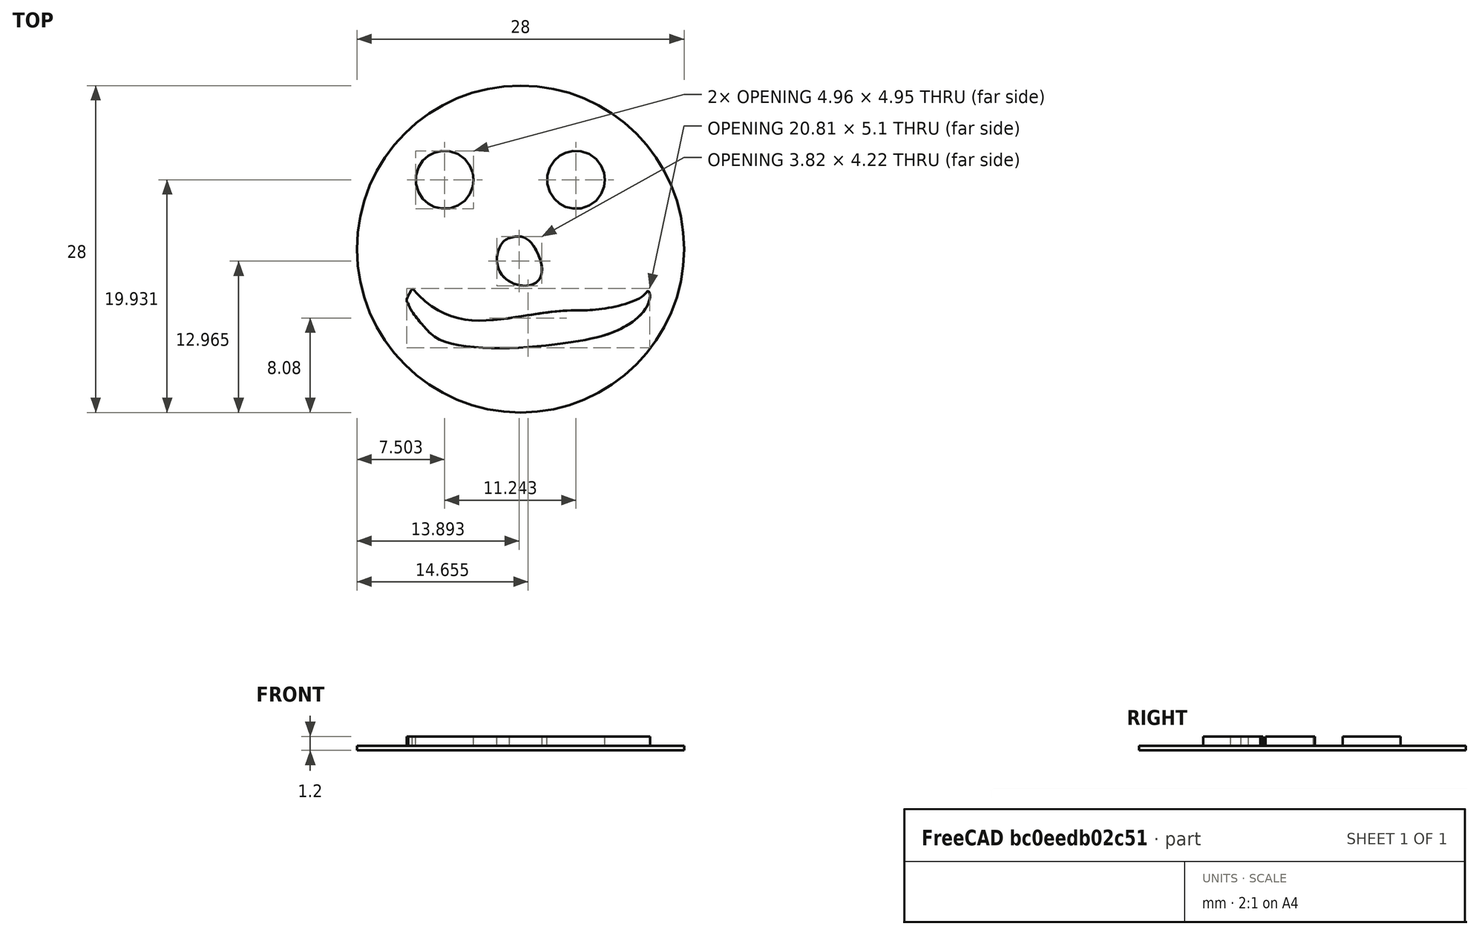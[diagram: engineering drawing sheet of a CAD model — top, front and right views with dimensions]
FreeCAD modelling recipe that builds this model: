
FCSTD DOCUMENT  (FreeCAD 0.18R14996 (Git))
Label: Medallion Face Test Rev B
License: All rights reserved
LicenseURL: http://en.wikipedia.org/wiki/All_rights_reserved
objects: Sketcher::SketchObject×2, PartDesign::Pad×2, Part::Part2DObjectPython×1, PartDesign::Body×1
note: 8 computed .brp shape members not serialized (recipe doc carries the construction recipe); baked Part::Feature solids carry a one-line shape summary decoded from their .brp

FEATURE [Sketcher::SketchObject] Sketch  label="Face Base Profile"
  MapMode = 5
  Support = -> [XY_Plane]
  sketch-geometry (1):
    g0: Circle CenterX=0 CenterY=0 CenterZ=0 NormalX=0 NormalY=0 NormalZ=1 AngleXU=0 Radius=14
  constraints (2):
    c: Coincident(g0,g-1)
    c: Radius(g0) = 14
FEATURE [PartDesign::Pad] Pad  label="Face Base"
  Length = 0.4
  Length2 = 100
  Profile = -> Sketch
  Type = 0
FEATURE [Sketcher::SketchObject] Sketch005
  Placement = pos=(-86.4048,117.218,0) rot=(0,0,1;0rad)
  sketch-geometry (11):
    g0: BSplineCurve PolesCount=7 KnotsCount=4 Degree=2 IsPeriodic=0
    g1: BSplineCurve PolesCount=4 KnotsCount=2 Degree=3 IsPeriodic=0
    g2: BSplineCurve PolesCount=4 KnotsCount=2 Degree=3 IsPeriodic=0
    g3: BSplineCurve PolesCount=4 KnotsCount=2 Degree=3 IsPeriodic=0
    g4: BSplineCurve PolesCount=7 KnotsCount=4 Degree=2 IsPeriodic=0
    g5: BSplineCurve PolesCount=4 KnotsCount=2 Degree=3 IsPeriodic=0
    g6: BSplineCurve PolesCount=4 KnotsCount=2 Degree=3 IsPeriodic=0
    g7: BSplineCurve PolesCount=4 KnotsCount=2 Degree=3 IsPeriodic=0
    g8: BSplineCurve PolesCount=4 KnotsCount=2 Degree=3 IsPeriodic=0
    g9: BSplineCurve PolesCount=4 KnotsCount=2 Degree=3 IsPeriodic=0
    g10: BSplineCurve PolesCount=4 KnotsCount=2 Degree=3 IsPeriodic=0
  constraints (9):
    c: Coincident(g1,g2)
    c: Coincident(g2,g3)
    c: Coincident(g3,g1)
    c: Coincident(g5,g6)
    c: Coincident(g6,g7)
    c: Coincident(g7,g8)
    c: Coincident(g8,g9)
    c: Coincident(g9,g10)
    c: Coincident(g10,g5)
FEATURE [Part::Part2DObjectPython] Clone2D  label="Sketch005 (2D)"  # Draft 2D object (typed FeaturePython)
  Fuse = false
  Objects = -> [Sketch005]
  Placement = pos=(-15.3624,20.0267,0) rot=(0,0,1;0rad)
  Scale = (0.18,0.18,0)
FEATURE [PartDesign::Pad] Pad001  label="Pattern Emboss"
  BaseFeature = -> Pad
  Length = 1.2
  Length2 = 100
  Profile = -> Clone2D
  Type = 0
FEATURE [PartDesign::Body] Body
  Group = -> [Sketch,Pad,Clone2D,Pad001]
  Origin = -> Origin
  Tip = -> Pad001
